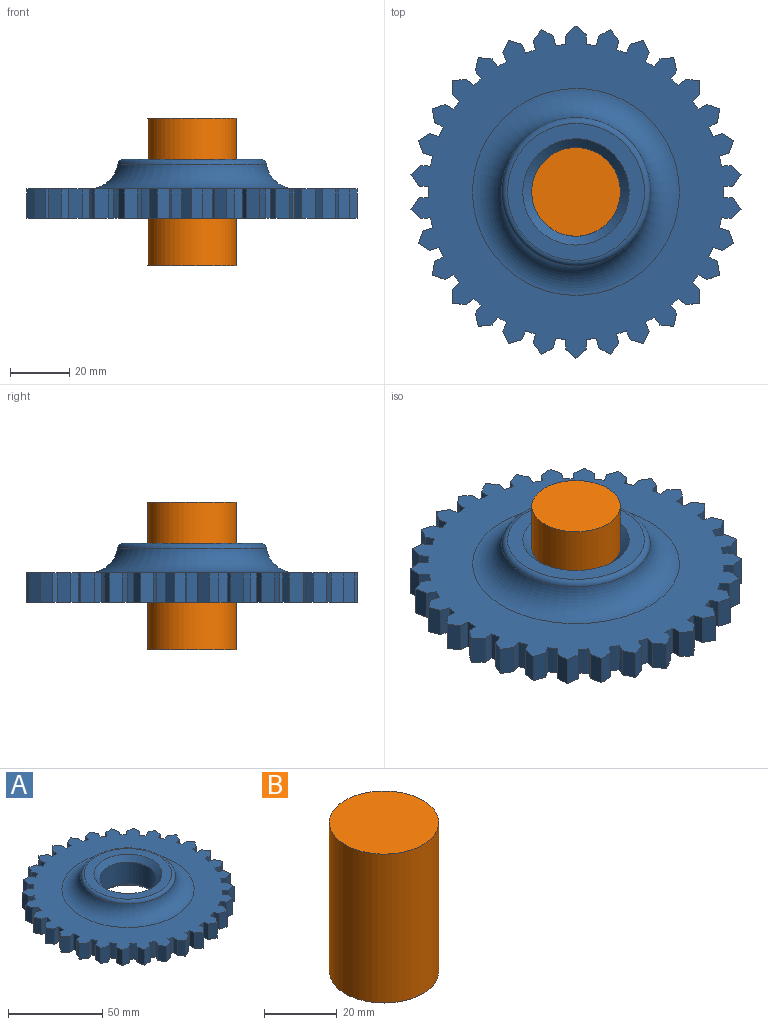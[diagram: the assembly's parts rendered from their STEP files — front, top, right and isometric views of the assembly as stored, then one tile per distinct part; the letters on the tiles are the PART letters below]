
ASSEMBLY  parts=2 mates=1
PART A: 159 faces, bbox 111.7x112.3x20 mm
  f0: cylinder r=50mm len=10mm, axis (0,0,-1), area 34.7mm2, adj f30,f31,f36,f150
  f1: cylinder r=50mm len=10mm, axis (0,0,-1), area 34.7mm2, adj f30,f31,f146,f152
  f2: cylinder r=50mm len=10mm, axis (0,0,-1), area 34.7mm2, adj f30,f31,f142,f148
  f3: cylinder r=50mm len=10mm, axis (0,0,-1), area 34.7mm2, adj f30,f31,f138,f144
  f4: cylinder r=50mm len=10mm, axis (0,0,-1), area 34.7mm2, adj f30,f31,f134,f140
  f5: cylinder r=50mm len=10mm, axis (0,0,-1), area 34.7mm2, adj f30,f31,f130,f136
  f6: cylinder r=50mm len=10mm, axis (0,0,-1), area 34.7mm2, adj f30,f31,f126,f132
  f7: cylinder r=50mm len=10mm, axis (0,0,-1), area 34.7mm2, adj f30,f31,f122,f128
  f8: cylinder r=50mm len=10mm, axis (0,0,-1), area 34.7mm2, adj f30,f31,f118,f124
  f9: cylinder r=50mm len=10mm, axis (0,0,-1), area 34.7mm2, adj f30,f31,f114,f120
  f10: cylinder r=50mm len=10mm, axis (0,0,-1), area 34.7mm2, adj f30,f31,f110,f116
  f11: cylinder r=50mm len=10mm, axis (0,0,-1), area 34.7mm2, adj f30,f31,f106,f112
  f12: cylinder r=50mm len=10mm, axis (0,0,-1), area 34.7mm2, adj f30,f31,f102,f108
  f13: cylinder r=50mm len=10mm, axis (0,0,-1), area 34.7mm2, adj f30,f31,f98,f104
  f14: cylinder r=50mm len=10mm, axis (0,0,-1), area 34.7mm2, adj f30,f31,f94,f100
  f15: cylinder r=50mm len=10mm, axis (0,0,-1), area 34.7mm2, adj f30,f31,f90,f96
  f16: cylinder r=50mm len=10mm, axis (0,0,-1), area 34.7mm2, adj f30,f31,f86,f92
  f17: cylinder r=50mm len=10mm, axis (0,0,-1), area 34.7mm2, adj f30,f31,f82,f88
  f18: cylinder r=50mm len=10mm, axis (0,0,-1), area 34.7mm2, adj f30,f31,f78,f84
  f19: cylinder r=50mm len=10mm, axis (0,0,-1), area 34.7mm2, adj f30,f31,f74,f80
  f20: cylinder r=50mm len=10mm, axis (0,0,-1), area 34.7mm2, adj f30,f31,f70,f76
  f21: cylinder r=50mm len=10mm, axis (0,0,-1), area 34.7mm2, adj f30,f31,f66,f72
  f22: cylinder r=50mm len=10mm, axis (0,0,-1), area 34.7mm2, adj f30,f31,f62,f68
  f23: cylinder r=50mm len=10mm, axis (0,0,-1), area 34.7mm2, adj f30,f31,f58,f64
  f24: cylinder r=50mm len=10mm, axis (0,0,-1), area 34.7mm2, adj f30,f31,f54,f60
  f25: cylinder r=50mm len=10mm, axis (0,0,-1), area 34.7mm2, adj f30,f31,f50,f56
  f26: cylinder r=50mm len=10mm, axis (0,0,-1), area 34.7mm2, adj f30,f31,f46,f52
  f27: cylinder r=50mm len=10mm, axis (0,0,-1), area 34.7mm2, adj f30,f31,f42,f48
  f28: cylinder r=50mm len=10mm, axis (0,0,-1), area 34.7mm2, adj f30,f31,f38,f44
  f29: cylinder r=50mm len=10mm, axis (0,0,-1), area 34.7mm2, adj f30,f31,f34,f40
  f30: plane 112.34x111.73mm, normal (0,0,1), area 4994.9mm2, adj f0,f1,f2,f3,f4,f5,f6,f7
  f31: plane 112.34x111.73mm, normal (0,0,-1), area 7825.5mm2, adj f0,f1,f2,f3,f4,f5,f6,f7
  f32: plane 46.34x46.34mm, normal (0,0,1), area 668.4mm2, adj f155,f156
  f33: cylinder r=15mm len=30mm, axis (0,0,1), area 1319.5mm2, adj f155,f157
  f34: plane 10x2.37mm, normal (-1,0,0), area 23.7mm2, adj f29,f30,f31,f158
  f35: plane 10x2.8mm, normal (-0.65,0.76,0), area 36.9mm2, adj f30,f31,f37,f158
  f36: plane 10x3.29mm, normal (1,0,0), area 32.9mm2, adj f0,f30,f31,f37
  f37: plane 10x3.5mm, normal (0.65,0.76,0), area 46.1mm2, adj f30,f31,f35,f36
  f38: plane 10x3.22mm, normal (-0.98,-0.21,0), area 32.9mm2, adj f28,f30,f31,f39
  f39: plane 10x3.66mm, normal (-0.79,0.61,0), area 46.1mm2, adj f30,f31,f38,f41
  f40: plane 10x3.22mm, normal (0.98,0.21,0), area 32.9mm2, adj f29,f30,f31,f41
  f41: plane 10x4.05mm, normal (0.48,0.88,0), area 46.1mm2, adj f30,f31,f39,f40
  f42: plane 10x3.01mm, normal (-0.91,-0.41,0), area 32.9mm2, adj f27,f30,f31,f43
  f43: plane 10x4.16mm, normal (-0.9,0.43,0), area 46.1mm2, adj f30,f31,f42,f45
  f44: plane 10x3.01mm, normal (0.91,0.41,0), area 32.9mm2, adj f28,f30,f31,f45
  f45: plane 10x4.42mm, normal (0.29,0.96,0), area 46.1mm2, adj f30,f31,f43,f44
  f46: plane 10x2.66mm, normal (-0.81,-0.59,0), area 32.9mm2, adj f26,f30,f31,f47
  f47: plane 10x4.48mm, normal (-0.97,0.23,0), area 46.1mm2, adj f30,f31,f46,f49
  f48: plane 10x2.66mm, normal (0.81,0.59,0), area 32.9mm2, adj f27,f30,f31,f49
  f49: plane 10x4.6mm, normal (0.08,1,0), area 46.1mm2, adj f30,f31,f47,f48
  f50: plane 10x2.45mm, normal (-0.67,-0.74,0), area 32.9mm2, adj f25,f30,f31,f51
  f51: plane 10x4.61mm, normal (-1,0.02,0), area 46.1mm2, adj f30,f31,f50,f53
  f52: plane 10x2.45mm, normal (0.67,0.74,0), area 32.9mm2, adj f26,f30,f31,f53
  f53: plane 10x4.57mm, normal (-0.13,0.99,0), area 46.1mm2, adj f30,f31,f51,f52
  f54: plane 10x2.85mm, normal (-0.5,-0.87,0), area 32.9mm2, adj f24,f30,f31,f55
  f55: plane 10x4.53mm, normal (-0.98,-0.18,0), area 46.1mm2, adj f30,f31,f54,f57
  f56: plane 10x2.85mm, normal (0.5,0.87,0), area 32.9mm2, adj f25,f30,f31,f57
  f57: plane 10x4.35mm, normal (-0.33,0.94,0), area 46.1mm2, adj f30,f31,f55,f56
  f58: plane 10x3.13mm, normal (-0.31,-0.95,0), area 32.9mm2, adj f23,f30,f31,f59
  f59: plane 10x4.26mm, normal (-0.92,-0.38,0), area 46.1mm2, adj f30,f31,f58,f61
  f60: plane 10x3.13mm, normal (0.31,0.95,0), area 32.9mm2, adj f24,f30,f31,f61
  f61: plane 10x3.93mm, normal (-0.52,0.85,0), area 46.1mm2, adj f30,f31,f59,f60
  f62: plane 10x3.28mm, normal (-0.1,-0.99,0), area 32.9mm2, adj f22,f30,f31,f63
  f63: plane 10x3.79mm, normal (-0.82,-0.57,0), area 46.1mm2, adj f30,f31,f62,f65
  f64: plane 10x3.28mm, normal (0.1,0.99,0), area 32.9mm2, adj f23,f30,f31,f65
  f65: plane 10x3.35mm, normal (-0.69,0.73,0), area 46.1mm2, adj f30,f31,f63,f64
  f66: plane 10x3.28mm, normal (0.1,-0.99,0), area 32.9mm2, adj f21,f30,f31,f67
  f67: plane 10x3.35mm, normal (-0.69,-0.73,0), area 46.1mm2, adj f30,f31,f66,f69
  f68: plane 10x3.28mm, normal (-0.1,0.99,0), area 32.9mm2, adj f22,f30,f31,f69
  f69: plane 10x3.79mm, normal (-0.82,0.57,0), area 46.1mm2, adj f30,f31,f67,f68
  f70: plane 10x3.13mm, normal (0.31,-0.95,0), area 32.9mm2, adj f20,f30,f31,f71
  f71: plane 10x3.93mm, normal (-0.52,-0.85,0), area 46.1mm2, adj f30,f31,f70,f73
  f72: plane 10x3.13mm, normal (-0.31,0.95,0), area 32.9mm2, adj f21,f30,f31,f73
  f73: plane 10x4.26mm, normal (-0.92,0.38,0), area 46.1mm2, adj f30,f31,f71,f72
  f74: plane 10x2.85mm, normal (0.5,-0.87,0), area 32.9mm2, adj f19,f30,f31,f75
  f75: plane 10x4.35mm, normal (-0.33,-0.94,0), area 46.1mm2, adj f30,f31,f74,f77
  f76: plane 10x2.85mm, normal (-0.5,0.87,0), area 32.9mm2, adj f20,f30,f31,f77
  f77: plane 10x4.53mm, normal (-0.98,0.18,0), area 46.1mm2, adj f30,f31,f75,f76
  f78: plane 10x2.45mm, normal (0.67,-0.74,0), area 32.9mm2, adj f18,f30,f31,f79
  f79: plane 10x4.57mm, normal (-0.13,-0.99,0), area 46.1mm2, adj f30,f31,f78,f81
  f80: plane 10x2.45mm, normal (-0.67,0.74,0), area 32.9mm2, adj f19,f30,f31,f81
  f81: plane 10x4.61mm, normal (-1,-0.02,0), area 46.1mm2, adj f30,f31,f79,f80
  f82: plane 10x2.66mm, normal (0.81,-0.59,0), area 32.9mm2, adj f17,f30,f31,f83
  f83: plane 10x4.6mm, normal (0.08,-1,0), area 46.1mm2, adj f30,f31,f82,f85
  f84: plane 10x2.66mm, normal (-0.81,0.59,0), area 32.9mm2, adj f18,f30,f31,f85
  f85: plane 10x4.48mm, normal (-0.97,-0.23,0), area 46.1mm2, adj f30,f31,f83,f84
  f86: plane 10x3.01mm, normal (0.91,-0.41,0), area 32.9mm2, adj f16,f30,f31,f87
  f87: plane 10x4.42mm, normal (0.29,-0.96,0), area 46.1mm2, adj f30,f31,f86,f89
  f88: plane 10x3.01mm, normal (-0.91,0.41,0), area 32.9mm2, adj f17,f30,f31,f89
  f89: plane 10x4.16mm, normal (-0.9,-0.43,0), area 46.1mm2, adj f30,f31,f87,f88
  f90: plane 10x3.22mm, normal (0.98,-0.21,0), area 32.9mm2, adj f15,f30,f31,f91
  f91: plane 10x4.05mm, normal (0.48,-0.88,0), area 46.1mm2, adj f30,f31,f90,f93
  f92: plane 10x3.22mm, normal (-0.98,0.21,0), area 32.9mm2, adj f16,f30,f31,f93
  f93: plane 10x3.66mm, normal (-0.79,-0.61,0), area 46.1mm2, adj f30,f31,f91,f92
  f94: plane 10x3.29mm, normal (1,0,0), area 32.9mm2, adj f14,f30,f31,f95
  f95: plane 10x3.5mm, normal (0.65,-0.76,0), area 46.1mm2, adj f30,f31,f94,f97
  f96: plane 10x3.29mm, normal (-1,0,0), area 32.9mm2, adj f15,f30,f31,f97
  f97: plane 10x3.5mm, normal (-0.65,-0.76,0), area 46.1mm2, adj f30,f31,f95,f96
  f98: plane 10x3.22mm, normal (0.98,0.21,0), area 32.9mm2, adj f13,f30,f31,f99
  f99: plane 10x3.66mm, normal (0.79,-0.61,0), area 46.1mm2, adj f30,f31,f98,f101
  f100: plane 10x3.22mm, normal (-0.98,-0.21,0), area 32.9mm2, adj f14,f30,f31,f101
  f101: plane 10x4.05mm, normal (-0.48,-0.88,0), area 46.1mm2, adj f30,f31,f99,f100
  f102: plane 10x3.01mm, normal (0.91,0.41,0), area 32.9mm2, adj f12,f30,f31,f103
  f103: plane 10x4.16mm, normal (0.9,-0.43,0), area 46.1mm2, adj f30,f31,f102,f105
  f104: plane 10x3.01mm, normal (-0.91,-0.41,0), area 32.9mm2, adj f13,f30,f31,f105
  f105: plane 10x4.42mm, normal (-0.29,-0.96,0), area 46.1mm2, adj f30,f31,f103,f104
  f106: plane 10x2.66mm, normal (0.81,0.59,0), area 32.9mm2, adj f11,f30,f31,f107
  f107: plane 10x4.48mm, normal (0.97,-0.23,0), area 46.1mm2, adj f30,f31,f106,f109
  f108: plane 10x2.66mm, normal (-0.81,-0.59,0), area 32.9mm2, adj f12,f30,f31,f109
  f109: plane 10x4.6mm, normal (-0.08,-1,0), area 46.1mm2, adj f30,f31,f107,f108
  f110: plane 10x2.45mm, normal (0.67,0.74,0), area 32.9mm2, adj f10,f30,f31,f111
  f111: plane 10x4.61mm, normal (1,-0.02,0), area 46.1mm2, adj f30,f31,f110,f113
  f112: plane 10x2.45mm, normal (-0.67,-0.74,0), area 32.9mm2, adj f11,f30,f31,f113
  f113: plane 10x4.57mm, normal (0.13,-0.99,0), area 46.1mm2, adj f30,f31,f111,f112
  f114: plane 10x2.85mm, normal (0.5,0.87,0), area 32.9mm2, adj f9,f30,f31,f115
  f115: plane 10x4.53mm, normal (0.98,0.18,0), area 46.1mm2, adj f30,f31,f114,f117
  f116: plane 10x2.85mm, normal (-0.5,-0.87,0), area 32.9mm2, adj f10,f30,f31,f117
  f117: plane 10x4.35mm, normal (0.33,-0.94,0), area 46.1mm2, adj f30,f31,f115,f116
  f118: plane 10x3.13mm, normal (0.31,0.95,0), area 32.9mm2, adj f8,f30,f31,f119
  f119: plane 10x4.26mm, normal (0.92,0.38,0), area 46.1mm2, adj f30,f31,f118,f121
  f120: plane 10x3.13mm, normal (-0.31,-0.95,0), area 32.9mm2, adj f9,f30,f31,f121
  f121: plane 10x3.93mm, normal (0.52,-0.85,0), area 46.1mm2, adj f30,f31,f119,f120
  f122: plane 10x3.28mm, normal (0.1,0.99,0), area 32.9mm2, adj f7,f30,f31,f123
  f123: plane 10x3.79mm, normal (0.82,0.57,0), area 46.1mm2, adj f30,f31,f122,f125
  f124: plane 10x3.28mm, normal (-0.1,-0.99,0), area 32.9mm2, adj f8,f30,f31,f125
  f125: plane 10x3.35mm, normal (0.69,-0.73,0), area 46.1mm2, adj f30,f31,f123,f124
  f126: plane 10x3.28mm, normal (-0.1,0.99,0), area 32.9mm2, adj f6,f30,f31,f127
  f127: plane 10x3.35mm, normal (0.69,0.73,0), area 46.1mm2, adj f30,f31,f126,f129
  f128: plane 10x3.28mm, normal (0.1,-0.99,0), area 32.9mm2, adj f7,f30,f31,f129
  f129: plane 10x3.79mm, normal (0.82,-0.57,0), area 46.1mm2, adj f30,f31,f127,f128
  f130: plane 10x3.13mm, normal (-0.31,0.95,0), area 32.9mm2, adj f5,f30,f31,f131
  f131: plane 10x3.93mm, normal (0.52,0.85,0), area 46.1mm2, adj f30,f31,f130,f133
  f132: plane 10x3.13mm, normal (0.31,-0.95,0), area 32.9mm2, adj f6,f30,f31,f133
  f133: plane 10x4.26mm, normal (0.92,-0.38,0), area 46.1mm2, adj f30,f31,f131,f132
  f134: plane 10x2.85mm, normal (-0.5,0.87,0), area 32.9mm2, adj f4,f30,f31,f135
  f135: plane 10x4.35mm, normal (0.33,0.94,0), area 46.1mm2, adj f30,f31,f134,f137
  f136: plane 10x2.85mm, normal (0.5,-0.87,0), area 32.9mm2, adj f5,f30,f31,f137
  f137: plane 10x4.53mm, normal (0.98,-0.18,0), area 46.1mm2, adj f30,f31,f135,f136
  f138: plane 10x2.45mm, normal (-0.67,0.74,0), area 32.9mm2, adj f3,f30,f31,f139
  f139: plane 10x4.57mm, normal (0.13,0.99,0), area 46.1mm2, adj f30,f31,f138,f141
  f140: plane 10x2.45mm, normal (0.67,-0.74,0), area 32.9mm2, adj f4,f30,f31,f141
  f141: plane 10x4.61mm, normal (1,0.02,0), area 46.1mm2, adj f30,f31,f139,f140
  f142: plane 10x2.66mm, normal (-0.81,0.59,0), area 32.9mm2, adj f2,f30,f31,f143
  f143: plane 10x4.6mm, normal (-0.08,1,0), area 46.1mm2, adj f30,f31,f142,f145
  f144: plane 10x2.66mm, normal (0.81,-0.59,0), area 32.9mm2, adj f3,f30,f31,f145
  f145: plane 10x4.48mm, normal (0.97,0.23,0), area 46.1mm2, adj f30,f31,f143,f144
  f146: plane 10x3.01mm, normal (-0.91,0.41,0), area 32.9mm2, adj f1,f30,f31,f147
  f147: plane 10x4.42mm, normal (-0.29,0.96,0), area 46.1mm2, adj f30,f31,f146,f149
  f148: plane 10x3.01mm, normal (0.91,-0.41,0), area 32.9mm2, adj f2,f30,f31,f149
  f149: plane 10x4.16mm, normal (0.9,0.43,0), area 46.1mm2, adj f30,f31,f147,f148
  f150: plane 10x3.22mm, normal (-0.98,0.21,0), area 32.9mm2, adj f0,f30,f31,f151
  f151: plane 10x4.05mm, normal (-0.48,0.88,0), area 46.1mm2, adj f30,f31,f150,f153
  f152: plane 10x3.22mm, normal (0.98,-0.21,0), area 32.9mm2, adj f1,f30,f31,f153
  f153: plane 10x3.66mm, normal (0.79,0.61,0), area 46.1mm2, adj f30,f31,f151,f152
  f154: torus R=35mm, axis (0,0,1), area 2562.5mm2, adj f30,f156
  f155: cone r=15mm half-angle=45deg, axis (0,0,1), area 439.8mm2, adj f32,f33
  f156: torus R=23.17mm, axis (0,0,-1), area 429.5mm2, adj f32,f154
  f157: cone r=15mm half-angle=45deg, axis (0,0,-1), area 439.8mm2, adj f31,f33
  f158: cylinder r=2mm len=10mm, axis (0,0,-1), area 17.2mm2, adj f30,f31,f34,f35
PART B: 3 faces, bbox 30x30x50 mm
  f0: cylinder r=15mm len=50mm, axis (0,0,-1), area 4712.4mm2, adj f1,f2
  f1: plane 30x30mm, normal (0,0,1), area 706.9mm2, adj f0
  f2: plane 30x30mm, normal (0,0,-1), area 706.9mm2, adj f0
PLACE A t=(20.49,-7.02,-7.38)mm
PLACE B t=(20.49,-7.02,-23.42)mm
MATE slider B.f0 <-> A.f33  axis (0,0,-1) through (20.49,-7.02,1.58)mm
